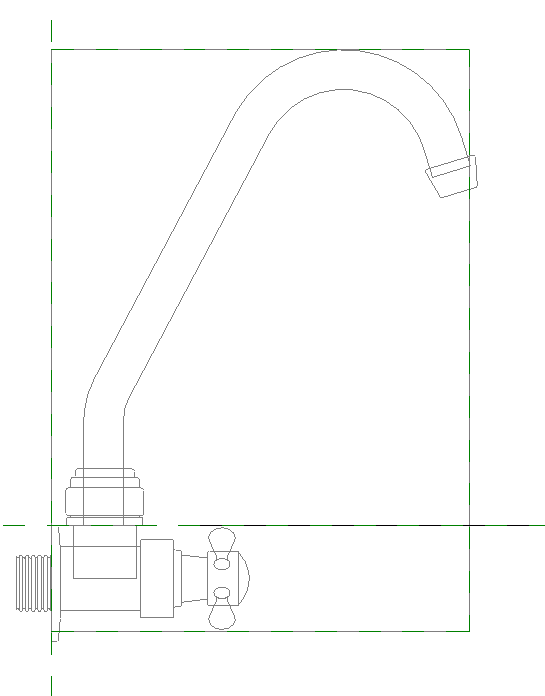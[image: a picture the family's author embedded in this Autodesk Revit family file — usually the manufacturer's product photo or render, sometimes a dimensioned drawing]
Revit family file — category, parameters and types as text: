
# Revit family: 415090001_Lavaplatos sencillo de pared CTA Balta
name_source: partatom
category: Plumbing Fixtures
units: mm (PartAtom-declared; Revit-internal decimal feet)

## family parameters
Always vertical = Yes
Cut with Voids When Loaded = No
Host = Wall
OmniClass Number = 23.31.11.00
OmniClass Title = Faucets
Part Type = Normal
Room Calculation Point = No
Round Connector Dimension = Use Diameter
Shared = No

## types (1)
- Lavaplatos sencillo de pared CTA Balta
    Alto = 329 mm  [stored 1.0794 ft]
    Ancho = 60 mm
    Capacidad de flujo = 8.3 L/min. (2.2 gpm) a 413 kPa (60 psi).
    Creado por = BIMBAU
    Default Elevation = 0 mm  [stored 0 ft]
    Description = Para la fabricación de este producto se utilizan materiales, equipos y tecnología de ultima generación que permiten ofrecer una grifería con los mas altos estándares de calidad.
    Diámetro abasto = 13 mm
    Fecha de creación = 29/04/2021
    Manufacturer = Corona.
    Material = Corona_Aluminio
    Material 2 = Corona_Acero inoxidable
    Model = Lavaplatos sencillo de pared CTA Balta.
    Normatividad = NTC 1644
    Presión máxima recomendada = 860 kPa (125 psi).
    Presión mínima recomendada = 138 kPa (20 psi).
    Profundidad = 237 mm  [stored 0.777559 ft]
    Recubrimientos = Resistente a la corrosión, pelado y decoloración por agua. Recubrimiento no tóxico. Condición de servicio recomendada, uso doméstico.
    Temperatura de uso = De 4° C a 66° C (40° F y 150° F).
    Vida útil = (Unidad de cierre): 500000 ciclos.

note: [stored X ft] marks values corroborated as IEEE doubles in the binary element streams (Revit-internal decimal feet)

## geometry (parser evidence)
native form markers: Sweep x7
no freeform markers — native parametric forms only
